# Revit family: 35941
name_source: partatom
category: Aparatos sanitarios
revit_build: Autodesk Revit 2018 (Build: 20170223_1515(x64)
units: mm (PartAtom-declared; Revit-internal decimal feet)

## family parameters
Anfitrión = Cara
Compartido = No
Corte con vacíos al cargar = No
Cota de conector redondo = Diámetro de uso
Número OmniClass = 23.45.55.14
Punto de cálculo de habitación = No
Tipo de pieza = Normal
Título OmniClass = Single Faucets

## types (1)
- 35941
    Accionamiento = Mediante pulsador
    CAUDAL = 8 l/min
    CIERRE = Automático en 30 seg.
    Comentarios de tipo = Cierre automático a los 30 ±10 s. Caudal de 8 l/min. Conexiones de entrada y salida 3/4". Apertura y seleccion  de temperatura por medio de un único pulsador. Cuerpo y pulsador en latón cromado. Componentes fabricados en materiales que soportan temperaturas de hasta 70ºC, para permitir la realización de desinfecciones térmicas anti-legionella. Cabeza intercambiable que comprende todo el sistema de temporización. Apertura por pulsador de mando único con selección de temperatura mediante giro de 180º. Válvulas antirretorno incorporadas conforme a la norma EN 1717, que impiden la intercomunicación del agua fría con la caliente. Posibilidad de posicionar el mando de regulación con un tope de temperatura. Suministrado con filtros. Tapa de acero inoxidable de 200 x 200 mm. Caja de empotrar y placa de fijación intermedia fabricada con protección antioxidante. Peso bruto de 2,580 kg.
    Conexión AC = Sí
    Conexión AF = Sí
    Código de montaje = C1030220
    Descripción = Grifo temporalizado mezclador de ducha para instalación empotrada con cuerpo de latón y pulsador ARTE Cromado.
    ENTRADA = Entrada/Salida 3/4"
    Elevación por defecto = 1219 mm
    Fabricante = PRESTO IBÉRICA
    Imagen de tipo = <Ninguno>
    Material = Latón
    Modelo = ALPA 90 ARTE-E
    PESO BRUTO = 1,100 Kg
    Presión Máxima = 8 bar
    REFERENCIA = 35941
    TIPO DE AGUA = Fría/Caliente
    Teléfono = (+34) 915 782 575
    URL = http://www.griferiasgalindo.com
